# Revit family: BAS-IP_Вызывная панель_AA-07BD
name_source: partatom
category: Устройства связи
units: mm (PartAtom-declared; Revit-internal decimal feet)

## family parameters
Всегда вертикально = Да
На основе рабочей плоскости = Нет
Общий = Нет
При загрузке вырезать с полостями = Нет
Размер круглого соединителя = Использовать диаметр
Сохранять ориентацию аннотаций = Нет
Тип детали = Нормальный
Точка расчета площади = Нет

## types (1)
- Серебристый
    ADSK_Единица измерения = шт.
    ADSK_Завод-изготовитель = BAS-IP
    ADSK_Количество = 1
    ADSK_Марка = AA-07BD Silver
    ADSK_Материал = Silver
    ADSK_Наименование = Многоабонентская IP вызывная панель с TFT экраном 4,3 дюйма
    IK-код = IK07
    Выходное видео = Half HD (1280 × 720), H.264 Main Profile
    Дисплей = 4,3” TFT, цветной с подсветкой
    Изготовитель = BAS-IP
    Камера = 1/4”
    Класс степени защиты = IP65
    Корпус = Алюминий
    Минимальная освещенность = 0,01 Люкс
    Ночная подсветка = 6 светодиодов
    Питание = +12 В постоянного тока
    Потребление питания = 6,5 Вт, в режиме ожидания - 3,6 Вт
    Размер под установку = 140 × 350 × 60 мм
    Размер самой панели = 155 × 375 × 55 мм
    Разрешение = 2 Мп
    Температурный режим = -40 – +65 °С
    Тип клавиатуры = Механические кнопки с подсветкой
    Тип панели = Многоабонентская
    Тип установки = Скрытого монтажа, накладной с BR-AA7
    Угол обзора камеры = 110° (по горизонтали)
    Цвет = Gray silver
    Цветовое решение = Серебристый
